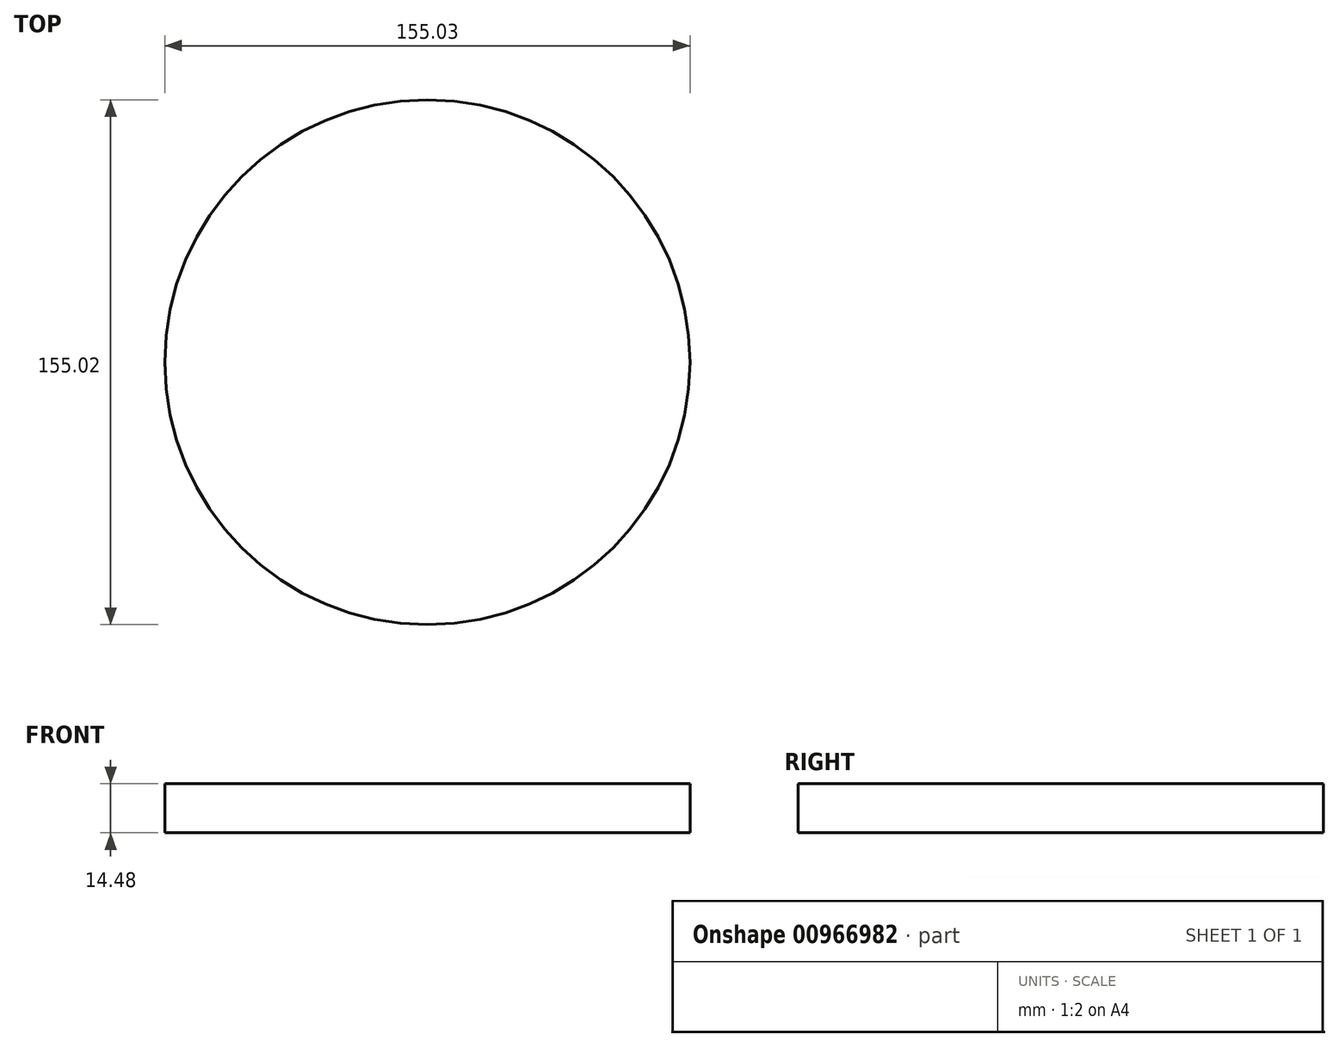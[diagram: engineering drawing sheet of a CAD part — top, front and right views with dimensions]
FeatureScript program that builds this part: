
annotation { "Feature Type Name" : "Feature", "Feature Type Description" : "" }
export const myFeature = defineFeature(function(context is Context, id is Id, definition is map)
    precondition{}
    {
        {
            var Q0;
            Q0=qCreatedBy(makeId("Top.planeOp"),FACE);
            var sketch = newSketch(context, id + "F0", { "sketchPlane" : qUnion([Q0])});
            skCircle(sketch, "E0", {"center": v(-5.08, 0) * mm, "radius": 77.51 * mm});
            skSolve(sketch);
        }
        {
            var Q0;
            Q0 = qSketchRegion(id + "F0", true);
            extrude(context, id + "F1", {"entities" : qUnion([Q0]), "depth" : 14.48 * mm, "offsetDistance" : 25.4 * mm});
        }
    });
